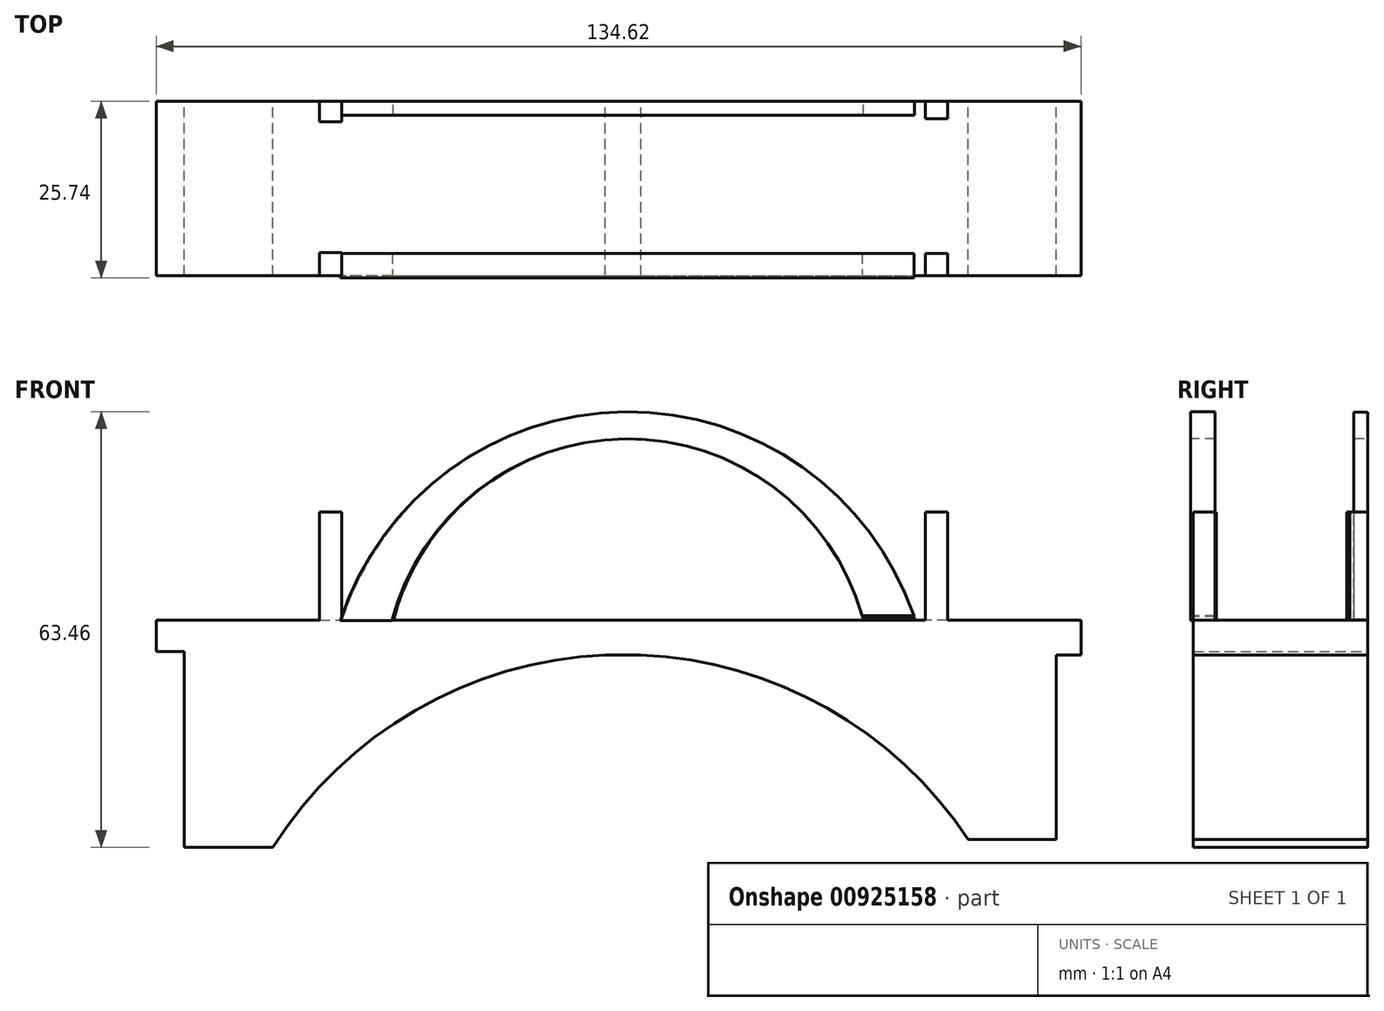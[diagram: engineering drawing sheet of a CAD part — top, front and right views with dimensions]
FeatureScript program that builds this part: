
annotation { "Feature Type Name" : "Feature", "Feature Type Description" : "" }
export const myFeature = defineFeature(function(context is Context, id is Id, definition is map)
    precondition{}
    {
        {
            var Q0;
            Q0=qCreatedBy(makeId("Top.planeOp"),FACE);
            cPlane(context, id + "F0", {"entities" : qUnion([Q0]), "cplaneType" : CPlaneType.OFFSET, "offset" : 25.4 * mm, "width" : 152.4 * mm, "height" : 152.4 * mm});
        }
        {
            var Q0;
            Q0=qCreatedBy(makeId("Front.planeOp"),FACE);
            cPlane(context, id + "F1", {"entities" : qUnion([Q0]), "cplaneType" : CPlaneType.OFFSET, "offset" : 12.95 * mm, "width" : 152.4 * mm, "height" : 152.4 * mm});
        }
        {
            var Q0;
            Q0=qCreatedBy(id+"F0.planeOp",FACE);
            cPlane(context, id + "F2", {"entities" : qUnion([Q0]), "cplaneType" : CPlaneType.OFFSET, "offset" : 25.4 * mm, "width" : 152.4 * mm, "height" : 152.4 * mm});
        }
        {
            var Q0;
            Q0=qCreatedBy(id+"F2.planeOp",FACE);
            var sketch = newSketch(context, id + "F3", { "sketchPlane" : qUnion([Q0])});
            skLineSegment(sketch, "E0.bottom", {"start": v(-60.4, 12.8) * mm, "end": v(66.6, 12.8) * mm});
            skLineSegment(sketch, "E0.top", {"start": v(-60.4, -12.6) * mm, "end": v(66.6, -12.6) * mm});
            skLineSegment(sketch, "E0.left", {"start": v(-60.4, 12.8) * mm, "end": v(-60.4, -12.6) * mm});
            skLineSegment(sketch, "E0.right", {"start": v(66.6, 12.8) * mm, "end": v(66.6, -12.6) * mm});
            skSolve(sketch);
        }
        {
            var Q0;
            Q0=makeQuery(id+"F3.imprint","IMPRINT",FACE,{"disambiguationData":[TD([[makeQuery(id+"F3.imprint","IMPRINT",EDGE,{"derivedFrom":sQuery(id+"F3.wireOp",EDGE,"E0.bottom")}),-1.0]])]});
            extrude(context, id + "F4", {"entities" : qUnion([Q0]), "depth" : 5.08 * mm, "offsetDistance" : 25.4 * mm});
        }
        {
            var Q0;
            Q0=makeQuery(id+"F4.opExtrude","CAP_FACE",FACE,{"disambiguationData":[OSD([sQuery(id+"F3.wireOp",EDGE,"E0.bottom"),sQuery(id+"F3.wireOp",EDGE,"E0.top"),sQuery(id+"F3.wireOp",EDGE,"E0.left"),sQuery(id+"F3.wireOp",EDGE,"E0.right")])],"isStart":false});
            var sketch = newSketch(context, id + "F5", { "sketchPlane" : qUnion([Q0])});
            skLineSegment(sketch, "E1.bottom", {"start": v(47.19, 12.8) * mm, "end": v(43.98, 12.8) * mm});
            skLineSegment(sketch, "E1.top", {"start": v(47.19, 10.21) * mm, "end": v(43.98, 10.21) * mm});
            skLineSegment(sketch, "E1.left", {"start": v(47.19, 12.8) * mm, "end": v(47.19, 10.21) * mm});
            skLineSegment(sketch, "E1.right", {"start": v(43.98, 12.8) * mm, "end": v(43.98, 10.21) * mm});
            skLineSegment(sketch, "E2.bottom", {"start": v(47.19, -12.6) * mm, "end": v(43.98, -12.6) * mm});
            skLineSegment(sketch, "E2.top", {"start": v(47.19, -9.4) * mm, "end": v(43.98, -9.4) * mm});
            skLineSegment(sketch, "E2.left", {"start": v(47.19, -12.6) * mm, "end": v(47.19, -9.4) * mm});
            skLineSegment(sketch, "E2.right", {"start": v(43.98, -12.6) * mm, "end": v(43.98, -9.4) * mm});
            skLineSegment(sketch, "E3.bottom", {"start": v(-44.21, 12.8) * mm, "end": v(-41.01, 12.8) * mm});
            skLineSegment(sketch, "E3.top", {"start": v(-44.21, 9.76) * mm, "end": v(-41.01, 9.76) * mm});
            skLineSegment(sketch, "E3.left", {"start": v(-44.21, 12.8) * mm, "end": v(-44.21, 9.76) * mm});
            skLineSegment(sketch, "E3.right", {"start": v(-41.01, 12.8) * mm, "end": v(-41.01, 9.76) * mm});
            skLineSegment(sketch, "E4.bottom", {"start": v(-41.01, -12.6) * mm, "end": v(-44.21, -12.6) * mm});
            skLineSegment(sketch, "E4.top", {"start": v(-41.01, -9.24) * mm, "end": v(-44.21, -9.24) * mm});
            skLineSegment(sketch, "E4.left", {"start": v(-41.01, -12.6) * mm, "end": v(-41.01, -9.24) * mm});
            skLineSegment(sketch, "E4.right", {"start": v(-44.21, -12.6) * mm, "end": v(-44.21, -9.24) * mm});
            skSolve(sketch);
        }
        {
            var Q0;
            Q0 = qSketchRegion(id + "F5", true);
            extrude(context, id + "F6", {"entities" : qUnion([Q0]), "operationType" : NewBodyOperationType.ADD, "depth" : 15.75 * mm, "offsetDistance" : 25.4 * mm});
        }
        {
            var Q0;
            Q0=makeQuery(id+"F6.boolean.opBoolean","MERGE",FACE,{"derivedFrom":[makeQuery(id+"F4.opExtrude","SWEPT_FACE",FACE,{"disambiguationData":[OSD([sQuery(id+"F3.wireOp",EDGE,"E0.bottom")])]}),makeQuery(id+"F6.opExtrude","SWEPT_FACE",FACE,{"disambiguationData":[OSD([sQuery(id+"F5.wireOp",EDGE,"E1.bottom")])]}),makeQuery(id+"F6.opExtrude","SWEPT_FACE",FACE,{"disambiguationData":[OSD([sQuery(id+"F5.wireOp",EDGE,"E3.bottom")])]})]});
            cPlane(context, id + "F7", {"entities" : qUnion([Q0]), "cplaneType" : CPlaneType.OFFSET, "offset" : 0 * mm, "width" : 152.4 * mm, "height" : 152.4 * mm});
        }
        {
            var Q0;
            Q0=qCreatedBy(id+"F7.planeOp",FACE);
            var sketch = newSketch(context, id + "F8", { "sketchPlane" : qUnion([Q0])});
            skLineSegment(sketch, "E5", {"start": v(63.91, 51.29) * mm, "end": v(63.91, 22.74) * mm});
            skLineSegment(sketch, "E6", {"start": v(-62.98, 52.44) * mm, "end": v(-62.98, 23.9) * mm});
            skLineSegment(sketch, "E7", {"start": v(-62.98, 23.9) * mm, "end": v(-50.2, 23.9) * mm});
            skLineSegment(sketch, "E8", {"start": v(63.91, 22.74) * mm, "end": v(51.03, 22.74) * mm});
            skArc(sketch, "E9", {"start": v(51.03, 22.74) * mm, "mid": v(0.73, 50.85) * mm, "end": v(-50.2, 23.9) * mm});
            skLineSegment(sketch, "E10", {"start": v(63.91, 51.29) * mm, "end": v(-62.98, 51.29) * mm});
            skSolve(sketch);
        }
        {
            var Q0;
            Q0 = qSketchRegion(id + "F8", true);
            extrude(context, id + "F9", {"entities" : qUnion([Q0]), "operationType" : NewBodyOperationType.ADD, "oppositeDirection" : true, "depth" : 25.4 * mm, "offsetDistance" : 25.4 * mm});
        }
        {
            var Q0;
            Q0=makeQuery(id+"F4.opExtrude","SWEPT_FACE",FACE,{"disambiguationData":[OSD([sQuery(id+"F3.wireOp",EDGE,"E0.left")])]});
            extrude(context, id + "F10", {"entities" : qUnion([Q0]), "operationType" : NewBodyOperationType.ADD, "depth" : 7.62 * mm, "offsetDistance" : 25.4 * mm});
        }
        {
            var Q0;
            Q0=qCreatedBy(id+"F7.planeOp",FACE);
            var sketch = newSketch(context, id + "F11", { "sketchPlane" : qUnion([Q0])});
            skArc(sketch, "E11", {"start": v(41.02, 55.84) * mm, "mid": v(-0.6, 86.16) * mm, "end": v(-42.4, 56.05) * mm});
            skLineSegment(sketch, "E12", {"start": v(-42.4, 56.05) * mm, "end": v(-34.91, 56.05) * mm});
            skLineSegment(sketch, "E13", {"start": v(41.02, 55.84) * mm, "end": v(33.49, 55.84) * mm});
            skArc(sketch, "E14", {"start": v(33.49, 55.84) * mm, "mid": v(-0.63, 82.3) * mm, "end": v(-34.91, 56.05) * mm});
            skSolve(sketch);
        }
        {
            var Q0;
            Q0=qCreatedBy(id+"F1.planeOp",FACE);
            var sketch = newSketch(context, id + "F12", { "sketchPlane" : qUnion([Q0])});
            skArc(sketch, "E15", {"start": v(42.28, 56.5) * mm, "mid": v(0.28, 86.2) * mm, "end": v(-41.2, 55.78) * mm});
            skLineSegment(sketch, "E16", {"start": v(42.28, 56.5) * mm, "end": v(34.75, 56.5) * mm});
            skLineSegment(sketch, "E17", {"start": v(-41.2, 55.78) * mm, "end": v(-33.68, 55.78) * mm});
            skArc(sketch, "E18", {"start": v(34.75, 56.5) * mm, "mid": v(0.26, 82.25) * mm, "end": v(-33.68, 55.78) * mm});
            skSolve(sketch);
        }
        {
            var Q0;
            Q0=makeQuery(id+"F12.imprint","IMPRINT",FACE,{"disambiguationData":[TD([[makeQuery(id+"F12.imprint","IMPRINT",EDGE,{"derivedFrom":sQuery(id+"F12.wireOp",EDGE,"E15")}),1.0]])]});
            extrude(context, id + "F13", {"entities" : qUnion([Q0]), "operationType" : NewBodyOperationType.ADD, "oppositeDirection" : true, "depth" : 3.56 * mm, "offsetDistance" : 25.4 * mm});
        }
        {
            var Q0;
            Q0=makeQuery(id+"F11.imprint","IMPRINT",FACE,{"disambiguationData":[TD([[makeQuery(id+"F11.imprint","IMPRINT",EDGE,{"derivedFrom":sQuery(id+"F11.wireOp",EDGE,"E11")}),1.0]])]});
            extrude(context, id + "F14", {"entities" : qUnion([Q0]), "oppositeDirection" : true, "depth" : 2.03 * mm, "offsetDistance" : 25.4 * mm});
        }
    });
